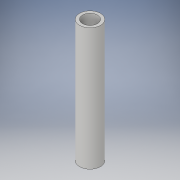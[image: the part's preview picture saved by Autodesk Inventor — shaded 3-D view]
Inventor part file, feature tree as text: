
AUTODESK INVENTOR PART (.ipt)
format: ipt  version: 2019.4 (Build 234330000, 330)  size: 94,208 bytes
history: native  units: mm
features: extrude x1, sketch x1
ambient origin geometry x8: Origin, YZ Plane, XZ Plane, XY Plane, X Axis, Y Axis, Z Axis, Center Point
bodies: Solid1 (feature_tree)
feature tree (2):
  extrude  "Extrusion1"  Depth=41.0mm
  sketch  "Sketch1"  dims[d0=5.0mm d1=7.0mm d2=41.0mm d3=0.0mm]
